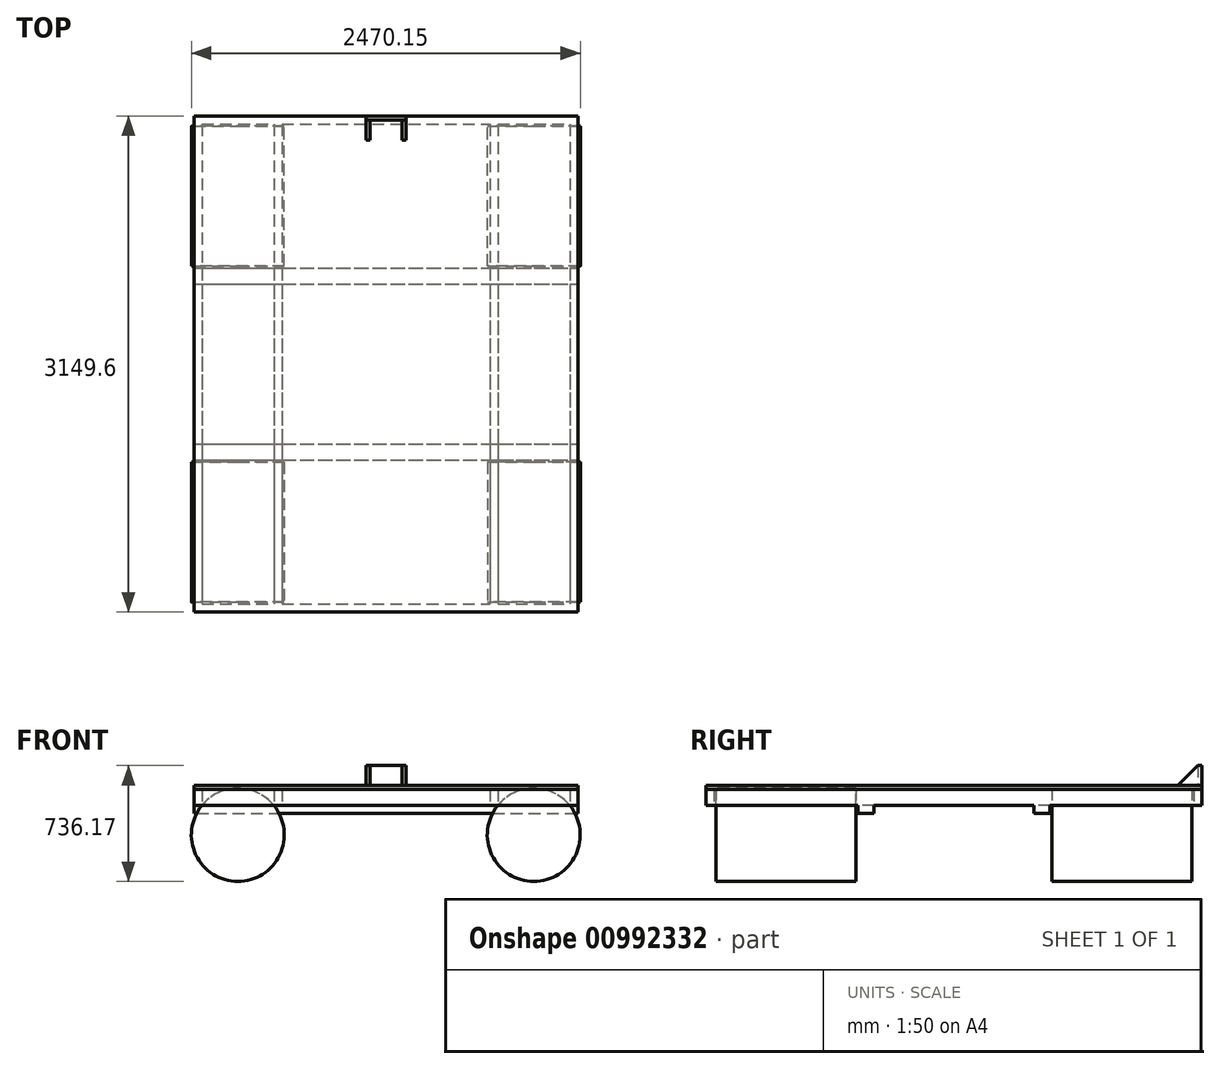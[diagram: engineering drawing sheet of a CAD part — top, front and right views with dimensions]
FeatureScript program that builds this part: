
annotation { "Feature Type Name" : "Feature", "Feature Type Description" : "" }
export const myFeature = defineFeature(function(context is Context, id is Id, definition is map)
    precondition{}
    {
        {
            var Q0;
            Q0=qCreatedBy(makeId("Top.planeOp"),FACE);
            var sketch = newSketch(context, id + "F0", { "sketchPlane" : qUnion([Q0])});
            skLineSegment(sketch, "E0.bottom", {"start": v(-2145.97, 2717.22) * mm, "end": v(-2095.17, 2717.22) * mm});
            skLineSegment(sketch, "E0.top", {"start": v(-2145.97, -330.78) * mm, "end": v(-2095.17, -330.78) * mm});
            skLineSegment(sketch, "E0.left", {"start": v(-2145.97, 2717.22) * mm, "end": v(-2145.97, -330.78) * mm});
            skLineSegment(sketch, "E0.right", {"start": v(-2095.17, 2717.22) * mm, "end": v(-2095.17, -330.78) * mm});
            skLineSegment(sketch, "E1.bottom", {"start": v(-1637.97, 2717.22) * mm, "end": v(-1587.17, 2717.22) * mm});
            skLineSegment(sketch, "E1.top", {"start": v(-1637.97, -330.78) * mm, "end": v(-1587.17, -330.78) * mm});
            skLineSegment(sketch, "E1.left", {"start": v(-1637.97, 2717.22) * mm, "end": v(-1637.97, -330.78) * mm});
            skLineSegment(sketch, "E1.right", {"start": v(-1587.17, 2717.22) * mm, "end": v(-1587.17, -330.78) * mm});
            skLineSegment(sketch, "E2.bottom", {"start": v(-266.37, 2717.22) * mm, "end": v(-215.57, 2717.22) * mm});
            skLineSegment(sketch, "E2.top", {"start": v(-266.37, -330.78) * mm, "end": v(-215.57, -330.78) * mm});
            skLineSegment(sketch, "E2.left", {"start": v(-266.37, 2717.22) * mm, "end": v(-266.37, -330.78) * mm});
            skLineSegment(sketch, "E2.right", {"start": v(-215.57, 2717.22) * mm, "end": v(-215.57, -330.78) * mm});
            skLineSegment(sketch, "E3.bottom", {"start": v(241.63, 2717.22) * mm, "end": v(292.43, 2717.22) * mm});
            skLineSegment(sketch, "E3.top", {"start": v(241.63, -330.78) * mm, "end": v(292.43, -330.78) * mm});
            skLineSegment(sketch, "E3.left", {"start": v(241.63, 2717.22) * mm, "end": v(241.63, -330.78) * mm});
            skLineSegment(sketch, "E3.right", {"start": v(292.43, 2717.22) * mm, "end": v(292.43, -330.78) * mm});
            skLineSegment(sketch, "E4.bottom", {"start": v(-2145.97, 2768.02) * mm, "end": v(292.43, 2768.02) * mm});
            skLineSegment(sketch, "E4.top", {"start": v(-2145.97, 2717.22) * mm, "end": v(292.43, 2717.22) * mm});
            skLineSegment(sketch, "E4.left", {"start": v(-2145.97, 2768.02) * mm, "end": v(-2145.97, 2717.22) * mm});
            skLineSegment(sketch, "E4.right", {"start": v(292.43, 2768.02) * mm, "end": v(292.43, 2717.22) * mm});
            skLineSegment(sketch, "E5.bottom", {"start": v(-2145.97, -330.78) * mm, "end": v(292.43, -330.78) * mm});
            skLineSegment(sketch, "E5.top", {"start": v(-2145.97, -381.58) * mm, "end": v(292.43, -381.58) * mm});
            skLineSegment(sketch, "E5.left", {"start": v(-2145.97, -330.78) * mm, "end": v(-2145.97, -381.58) * mm});
            skLineSegment(sketch, "E5.right", {"start": v(292.43, -330.78) * mm, "end": v(292.43, -381.58) * mm});
            skLineSegment(sketch, "E6.bottom", {"start": v(-1079.17, 2717.22) * mm, "end": v(-1028.37, 2717.22) * mm});
            skLineSegment(sketch, "E6.top", {"start": v(-1079.17, -330.78) * mm, "end": v(-1028.37, -330.78) * mm});
            skLineSegment(sketch, "E6.left", {"start": v(-1079.17, 2717.22) * mm, "end": v(-1079.17, -330.78) * mm});
            skLineSegment(sketch, "E6.right", {"start": v(-1028.37, 2717.22) * mm, "end": v(-1028.37, -330.78) * mm});
            skLineSegment(sketch, "E7.bottom", {"start": v(-825.17, 2717.22) * mm, "end": v(-774.37, 2717.22) * mm});
            skLineSegment(sketch, "E7.top", {"start": v(-825.17, -330.78) * mm, "end": v(-774.37, -330.78) * mm});
            skLineSegment(sketch, "E7.left", {"start": v(-825.17, 2717.22) * mm, "end": v(-825.17, -330.78) * mm});
            skLineSegment(sketch, "E7.right", {"start": v(-774.37, 2717.22) * mm, "end": v(-774.37, -330.78) * mm});
            skSolve(sketch);
        }
        {
            var Q0;
            Q0 = qSketchRegion(id + "F0", true);
            var Q1;
            {var subQ0=sQuery(id+"F0.wireOp",EDGE,"E1.left");Q1=makeQuery(id+"F0.imprint","IMPRINT",FACE,{"disambiguationData":[TD([[makeQuery(id+"F0.imprint","IMPRINT",EDGE,{"derivedFrom":subQ0}),1.0]])]});}
            var Q2;
            Q2=makeQuery(id+"F0.imprint","IMPRINT",FACE,{"disambiguationData":[TD([[makeQuery(id+"F0.imprint","IMPRINT",EDGE,{"derivedFrom":sQuery(id+"F0.wireOp",EDGE,"E6.bottom")}),-1.0]])]});
            var Q3;
            Q3=makeQuery(id+"F0.imprint","IMPRINT",FACE,{"disambiguationData":[TD([[makeQuery(id+"F0.imprint","IMPRINT",EDGE,{"derivedFrom":sQuery(id+"F0.wireOp",EDGE,"E7.bottom")}),-1.0]])]});
            var Q4;
            {var subQ0=sQuery(id+"F0.wireOp",EDGE,"E2.left");Q4=makeQuery(id+"F0.imprint","IMPRINT",FACE,{"disambiguationData":[TD([[makeQuery(id+"F0.imprint","IMPRINT",EDGE,{"derivedFrom":subQ0}),1.0]])]});}
            extrude(context, id + "F1", {"entities" : qUnion([Q0, Q1, Q2, Q3, Q4]), "depth" : 101.6 * mm, "offsetDistance" : 25.4 * mm});
        }
        {
            var Q0;
            Q0=makeQuery(id+"F1.opExtrude","SWEPT_FACE",FACE,{"disambiguationData":[OSD([sQuery(id+"F0.wireOp",EDGE,"E3.left")])]});
            cPlane(context, id + "F2", {"entities" : qUnion([Q0]), "cplaneType" : CPlaneType.OFFSET, "offset" : 50.8 * mm, "oppositeDirection" : true, "width" : 152.4 * mm, "height" : 152.4 * mm});
        }
        {
            var Q0;
            Q0=makeQuery(id+"F1.opExtrude","SWEPT_FACE",FACE,{"disambiguationData":[OSD([sQuery(id+"F0.wireOp",EDGE,"E5.top")])]});
            cPlane(context, id + "F3", {"entities" : qUnion([Q0]), "cplaneType" : CPlaneType.OFFSET, "offset" : 63.5 * mm, "oppositeDirection" : true, "width" : 152.4 * mm, "height" : 152.4 * mm});
        }
        {
            var Q0;
            Q0=makeQuery(id+"F1.opExtrude","SWEPT_FACE",FACE,{"disambiguationData":[OSD([sQuery(id+"F0.wireOp",EDGE,"E4.bottom")])]});
            cPlane(context, id + "F4", {"entities" : qUnion([Q0]), "cplaneType" : CPlaneType.OFFSET, "offset" : 63.5 * mm, "oppositeDirection" : true, "width" : 152.4 * mm, "height" : 152.4 * mm});
        }
        {
            var Q0;
            Q0=qCreatedBy(id+"F3.planeOp",FACE);
            var sketch = newSketch(context, id + "F5", { "sketchPlane" : qUnion([Q0])});
            skCircle(sketch, "E8", {"center": v(-1866.57, -186.9) * mm, "radius": 295.28 * mm});
            skCircle(sketch, "E9", {"center": v(13.03, -186.9) * mm, "radius": 295.28 * mm});
            skSolve(sketch);
        }
        {
            var Q0;
            Q0=qCreatedBy(id+"F2.planeOp",FACE);
            var sketch = newSketch(context, id + "F6", { "sketchPlane" : qUnion([Q0])});
            skLineSegment(sketch, "E10.bottom", {"start": v(-1802.82, 0) * mm, "end": v(-1701.22, 0) * mm});
            skLineSegment(sketch, "E10.top", {"start": v(-1802.82, -50.8) * mm, "end": v(-1701.22, -50.8) * mm});
            skLineSegment(sketch, "E10.left", {"start": v(-1802.82, 0) * mm, "end": v(-1802.82, -50.8) * mm});
            skLineSegment(sketch, "E10.right", {"start": v(-1701.22, 0) * mm, "end": v(-1701.22, -50.8) * mm});
            skLineSegment(sketch, "E11.bottom", {"start": v(-685.22, 0) * mm, "end": v(-583.62, 0) * mm});
            skLineSegment(sketch, "E11.top", {"start": v(-685.22, -50.8) * mm, "end": v(-583.62, -50.8) * mm});
            skLineSegment(sketch, "E11.left", {"start": v(-685.22, 0) * mm, "end": v(-685.22, -50.8) * mm});
            skLineSegment(sketch, "E11.right", {"start": v(-583.62, 0) * mm, "end": v(-583.62, -50.8) * mm});
            skSolve(sketch);
        }
        {
            var Q0;
            Q0=makeQuery(id+"F6.imprint","IMPRINT",FACE,{"disambiguationData":[TD([[makeQuery(id+"F6.imprint","IMPRINT",EDGE,{"derivedFrom":sQuery(id+"F6.wireOp",EDGE,"E11.bottom")}),-1.0]])]});
            var Q1;
            Q1=makeQuery(id+"F6.imprint","IMPRINT",FACE,{"disambiguationData":[TD([[makeQuery(id+"F6.imprint","IMPRINT",EDGE,{"derivedFrom":sQuery(id+"F6.wireOp",EDGE,"E10.bottom")}),-1.0]])]});
            extrude(context, id + "F7", {"entities" : qUnion([Q0, Q1]), "operationType" : NewBodyOperationType.ADD, "depth" : 2438.4 * mm, "offsetDistance" : 25.4 * mm});
        }
        {
            var Q0;
            Q0=makeQuery(id+"F5.imprint","IMPRINT",FACE,{"disambiguationData":[TD([[makeQuery(id+"F5.imprint","IMPRINT",EDGE,{"derivedFrom":sQuery(id+"F5.wireOp",EDGE,"E9")}),1.0]])]});
            var Q1;
            Q1=makeQuery(id+"F5.imprint","IMPRINT",FACE,{"disambiguationData":[TD([[makeQuery(id+"F5.imprint","IMPRINT",EDGE,{"derivedFrom":sQuery(id+"F5.wireOp",EDGE,"E8")}),1.0]])]});
            extrude(context, id + "F8", {"entities" : qUnion([Q0, Q1]), "operationType" : NewBodyOperationType.ADD, "oppositeDirection" : true, "depth" : 889 * mm, "offsetDistance" : 25.4 * mm});
        }
        {
            var Q0;
            Q0=qCreatedBy(id+"F4.planeOp",FACE);
            var sketch = newSketch(context, id + "F9", { "sketchPlane" : qUnion([Q0])});
            skCircle(sketch, "E12.0.0", {"center": v(-13.03, -186.9) * mm, "radius": 295.28 * mm});
            skCircle(sketch, "E13.0.0", {"center": v(1866.57, -186.9) * mm, "radius": 295.28 * mm});
            skSolve(sketch);
        }
        {
            var Q0;
            Q0=makeQuery(id+"F9.imprint","IMPRINT",FACE,{"disambiguationData":[TD([[makeQuery(id+"F9.imprint","IMPRINT",EDGE,{"derivedFrom":sQuery(id+"F9.wireOp",EDGE,"E12.0.0")}),1.0]])]});
            var Q1;
            Q1=makeQuery(id+"F9.imprint","IMPRINT",FACE,{"disambiguationData":[TD([[makeQuery(id+"F9.imprint","IMPRINT",EDGE,{"derivedFrom":sQuery(id+"F9.wireOp",EDGE,"E13.0.0")}),1.0]])]});
            extrude(context, id + "F10", {"entities" : qUnion([Q0, Q1]), "operationType" : NewBodyOperationType.ADD, "oppositeDirection" : true, "depth" : 889 * mm, "offsetDistance" : 25.4 * mm});
        }
        {
            var Q0;
            Q0=makeQuery(id+"F1.opExtrude","CAP_FACE",FACE,{"disambiguationData":[OSD([sQuery(id+"F0.wireOp",EDGE,"E0.left"),sQuery(id+"F0.wireOp",EDGE,"E0.right"),sQuery(id+"F0.wireOp",EDGE,"E1.left"),sQuery(id+"F0.wireOp",EDGE,"E1.right"),sQuery(id+"F0.wireOp",EDGE,"E2.left"),sQuery(id+"F0.wireOp",EDGE,"E2.right"),sQuery(id+"F0.wireOp",EDGE,"E3.left"),sQuery(id+"F0.wireOp",EDGE,"E3.right"),sQuery(id+"F0.wireOp",EDGE,"E4.bottom"),sQuery(id+"F0.wireOp",EDGE,"E4.top"),sQuery(id+"F0.wireOp",EDGE,"E4.left"),sQuery(id+"F0.wireOp",EDGE,"E4.right"),sQuery(id+"F0.wireOp",EDGE,"E5.bottom"),sQuery(id+"F0.wireOp",EDGE,"E5.top"),sQuery(id+"F0.wireOp",EDGE,"E5.left"),sQuery(id+"F0.wireOp",EDGE,"E5.right"),sQuery(id+"F0.wireOp",EDGE,"E6.left"),sQuery(id+"F0.wireOp",EDGE,"E6.right"),sQuery(id+"F0.wireOp",EDGE,"E7.left"),sQuery(id+"F0.wireOp",EDGE,"E7.right")])],"isStart":false});
            cPlane(context, id + "F11", {"entities" : qUnion([Q0]), "cplaneType" : CPlaneType.OFFSET, "offset" : 0 * mm, "width" : 152.4 * mm, "height" : 152.4 * mm});
        }
        {
            var Q0;
            Q0=qCreatedBy(id+"F11.planeOp",FACE);
            var sketch = newSketch(context, id + "F12", { "sketchPlane" : qUnion([Q0])});
            skLineSegment(sketch, "E14.bottom", {"start": v(-2145.97, 2768.02) * mm, "end": v(292.43, 2768.02) * mm});
            skLineSegment(sketch, "E14.top", {"start": v(-2145.97, -381.58) * mm, "end": v(292.43, -381.58) * mm});
            skLineSegment(sketch, "E14.left", {"start": v(-2145.97, 2768.02) * mm, "end": v(-2145.97, -381.58) * mm});
            skLineSegment(sketch, "E14.right", {"start": v(292.43, 2768.02) * mm, "end": v(292.43, -381.58) * mm});
            skLineSegment(sketch, "E15", {"start": v(-926.77, -381.58) * mm, "end": v(-926.77, 2768.02) * mm});
            skLineSegment(sketch, "E16.bottom", {"start": v(-1028.37, 2768.02) * mm, "end": v(-799.77, 2768.02) * mm});
            skLineSegment(sketch, "E17.bottom", {"start": v(-1053.77, 2742.62) * mm, "end": v(-799.77, 2742.62) * mm});
            skLineSegment(sketch, "E17.top", {"start": v(-1053.77, 2768.02) * mm, "end": v(-799.77, 2768.02) * mm});
            skLineSegment(sketch, "E17.left", {"start": v(-1053.77, 2742.62) * mm, "end": v(-1053.77, 2768.02) * mm});
            skLineSegment(sketch, "E17.right", {"start": v(-799.77, 2742.62) * mm, "end": v(-799.77, 2768.02) * mm});
            skSolve(sketch);
        }
        {
            var Q0;
            Q0 = qSketchRegion(id + "F12", true);
            extrude(context, id + "F13", {"entities" : qUnion([Q0]), "depth" : 25.4 * mm, "offsetDistance" : 25.4 * mm});
        }
        {
            var Q0;
            {var subQ5=sQuery(id+"F12.wireOp",EDGE,"E17.left");Q0=makeQuery(id+"F12.imprint","IMPRINT",FACE,{"disambiguationData":[TD([[makeQuery(id+"F12.imprint","IMPRINT",EDGE,{"derivedFrom":subQ5}),-1.0]])]});}
            var Q1;
            {var subQ5=sQuery(id+"F12.wireOp",EDGE,"E17.right");Q1=makeQuery(id+"F12.imprint","IMPRINT",FACE,{"disambiguationData":[TD([[makeQuery(id+"F12.imprint","IMPRINT",EDGE,{"derivedFrom":subQ5}),1.0]])]});}
            extrude(context, id + "F14", {"entities" : qUnion([Q0, Q1]), "depth" : 152.4 * mm, "offsetDistance" : 25.4 * mm});
        }
        {
            var Q0;
            Q0=makeQuery(id+"F14.opExtrude","SWEPT_FACE",FACE,{"disambiguationData":[OSD([sQuery(id+"F12.wireOp",EDGE,"E17.right")])]});
            var sketch = newSketch(context, id + "F15", { "sketchPlane" : qUnion([Q0])});
            skLineSegment(sketch, "E18", {"start": v(2742.62, 254) * mm, "end": v(2615.62, 127) * mm});
            skLineSegment(sketch, "E19", {"start": v(2615.62, 127) * mm, "end": v(2742.62, 127) * mm});
            skSolve(sketch);
        }
        {
            var Q0;
            {var subQ0=sQuery(id+"F15.wireOp",EDGE,"E18");Q0=makeQuery(id+"F15.imprint","IMPRINT",FACE,{"disambiguationData":[TD([[makeQuery(id+"F15.imprint","IMPRINT",EDGE,{"derivedFrom":subQ0}),1.0]])]});}
            extrude(context, id + "F16", {"entities" : qUnion([Q0]), "operationType" : NewBodyOperationType.ADD, "oppositeDirection" : true, "depth" : 25.4 * mm, "offsetDistance" : 25.4 * mm});
        }
        {
            var Q0;
            Q0=makeQuery(id+"F14.opExtrude","SWEPT_FACE",FACE,{"disambiguationData":[OSD([sQuery(id+"F12.wireOp",EDGE,"E17.left")])]});
            var sketch = newSketch(context, id + "F17", { "sketchPlane" : qUnion([Q0])});
            skLineSegment(sketch, "E20.0.0", {"start": v(-2615.62, 127) * mm, "end": v(-2742.62, 254) * mm});
            skLineSegment(sketch, "E20.0.1", {"start": v(-2742.62, 254) * mm, "end": v(-2742.62, 127) * mm});
            skLineSegment(sketch, "E20.0.2", {"start": v(-2742.62, 127) * mm, "end": v(-2615.62, 127) * mm});
            skSolve(sketch);
        }
        {
            var Q0;
            Q0=makeQuery(id+"F17.imprint","IMPRINT",FACE,{"disambiguationData":[TD([[makeQuery(id+"F17.imprint","IMPRINT",EDGE,{"derivedFrom":sQuery(id+"F17.wireOp",EDGE,"E20.0.0")}),1.0]])]});
            extrude(context, id + "F18", {"entities" : qUnion([Q0]), "operationType" : NewBodyOperationType.ADD, "oppositeDirection" : true, "depth" : 25.4 * mm, "offsetDistance" : 25.4 * mm});
        }
    });
